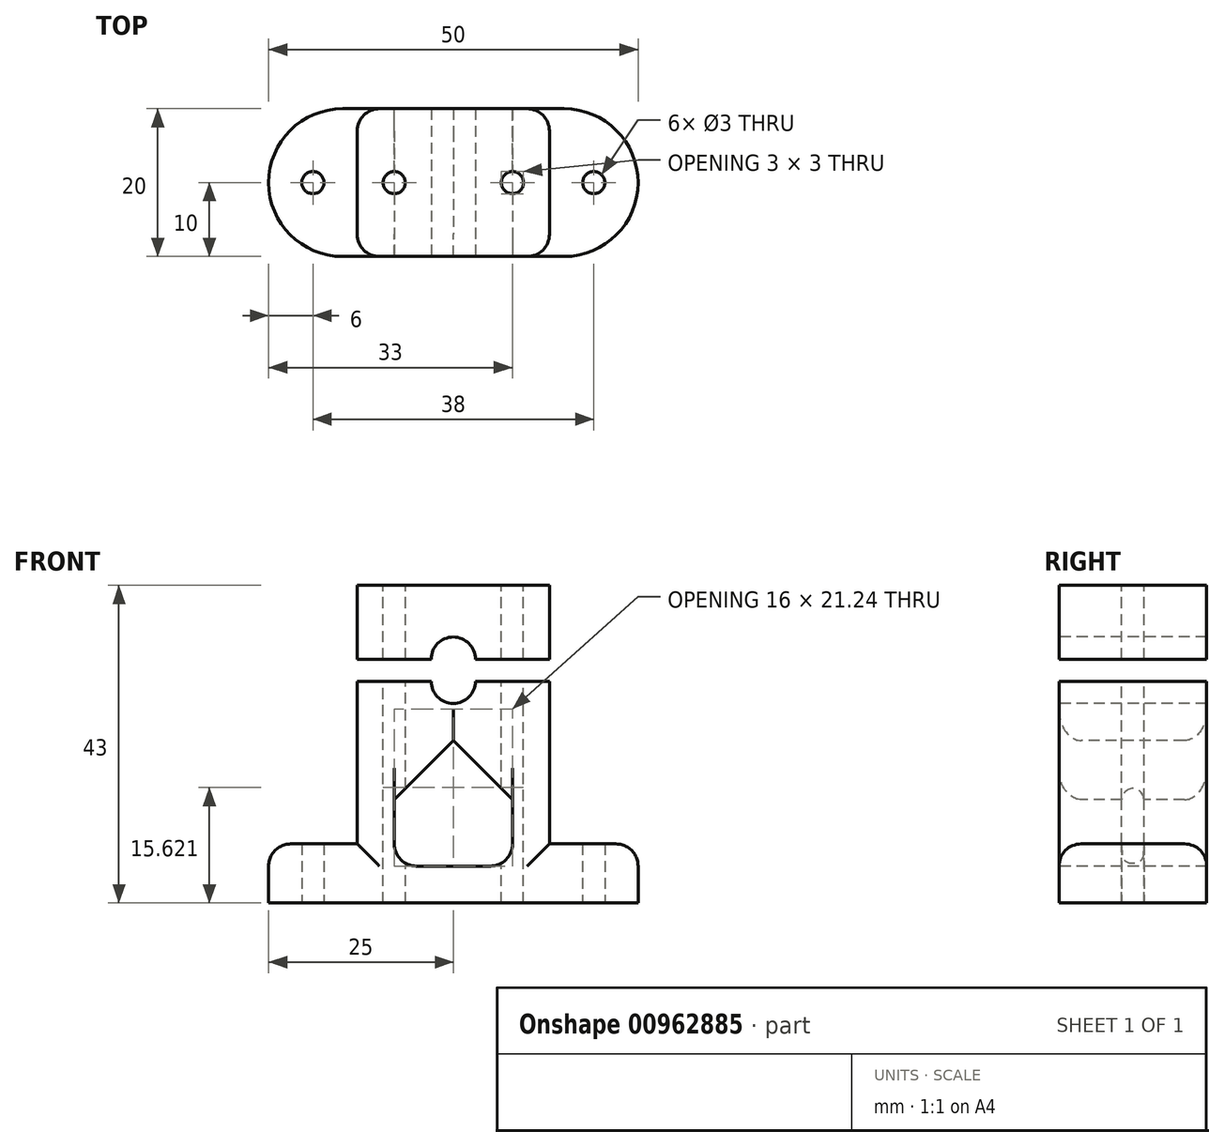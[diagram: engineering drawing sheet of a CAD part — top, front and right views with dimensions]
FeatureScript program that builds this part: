
annotation { "Feature Type Name" : "Feature", "Feature Type Description" : "" }
export const myFeature = defineFeature(function(context is Context, id is Id, definition is map)
    precondition{}
    {
        {
            var Q0;
            Q0=qCreatedBy(makeId("Top.planeOp"),FACE);
            var sketch = newSketch(context, id + "F0", { "sketchPlane" : qUnion([Q0])});
            skLineSegment(sketch, "E0", {"start": v(0, 0) * mm, "end": v(50, 0) * mm});
            skLineSegment(sketch, "E1", {"start": v(50, 0) * mm, "end": v(50, 8) * mm});
            skLineSegment(sketch, "E2", {"start": v(50, 8) * mm, "end": v(38, 8) * mm});
            skLineSegment(sketch, "E3", {"start": v(38, 8) * mm, "end": v(38, 30) * mm});
            skLineSegment(sketch, "E4", {"start": v(38, 30) * mm, "end": v(28, 30) * mm});
            skLineSegment(sketch, "E5", {"start": v(0, 0) * mm, "end": v(0, 8) * mm});
            skLineSegment(sketch, "E6", {"start": v(0, 8) * mm, "end": v(12, 8) * mm});
            skLineSegment(sketch, "E7", {"start": v(12, 8) * mm, "end": v(12, 30) * mm});
            skLineSegment(sketch, "E8", {"start": v(12, 30) * mm, "end": v(22, 30) * mm});
            skArc(sketch, "E9", {"start": v(22, 30) * mm, "mid": v(25, 27) * mm, "end": v(28, 30) * mm});
            skLineSegment(sketch, "E10", {"start": v(25, 30) * mm, "end": v(25, 0) * mm, "construction": true});
            skLineSegment(sketch, "E11", {"start": v(25, 22) * mm, "end": v(33, 14) * mm});
            skLineSegment(sketch, "E12", {"start": v(33, 14) * mm, "end": v(33, 5) * mm});
            skLineSegment(sketch, "E13", {"start": v(33, 5) * mm, "end": v(17, 5) * mm});
            skLineSegment(sketch, "E14", {"start": v(17, 5) * mm, "end": v(17, 14) * mm});
            skLineSegment(sketch, "E15", {"start": v(17, 14) * mm, "end": v(25, 22) * mm});
            skLineSegment(sketch, "E16", {"start": v(12, 33) * mm, "end": v(12, 43) * mm});
            skLineSegment(sketch, "E17", {"start": v(12, 43) * mm, "end": v(38, 43) * mm});
            skLineSegment(sketch, "E18", {"start": v(38, 43) * mm, "end": v(38, 33) * mm});
            skLineSegment(sketch, "E19", {"start": v(38, 33) * mm, "end": v(28, 33) * mm});
            skArc(sketch, "E20", {"start": v(28, 33) * mm, "mid": v(25, 36) * mm, "end": v(22, 33) * mm});
            skLineSegment(sketch, "E21.trimOffspring", {"start": v(22, 33) * mm, "end": v(12, 33) * mm});
            skSolve(sketch);
        }
        {
            var Q0;
            Q0 = qSketchRegion(id + "F0", true);
            extrude(context, id + "F1", {"entities" : qUnion([Q0]), "oppositeDirection" : true, "depth" : 20 * mm, "offsetDistance" : 25 * mm});
        }
        {
            var Q0;
            Q0=makeQuery(id+"F1.opExtrude","SWEPT_FACE",FACE,{"disambiguationData":[OSD([sQuery(id+"F0.wireOp",EDGE,"E0")])]});
            var sketch = newSketch(context, id + "F2", { "sketchPlane" : qUnion([Q0])});
            skCircle(sketch, "E22", {"center": v(6, -10) * mm, "radius": 1.5 * mm});
            skCircle(sketch, "E23", {"center": v(44, -10) * mm, "radius": 1.5 * mm});
            skLineSegment(sketch, "E24", {"start": v(0, -10) * mm, "end": v(50, -10) * mm, "construction": true});
            skSolve(sketch);
        }
        {
            var Q0;
            Q0=makeQuery(id+"F2.imprint","IMPRINT",FACE,{"disambiguationData":[TD([[makeQuery(id+"F2.imprint","IMPRINT",EDGE,{"derivedFrom":sQuery(id+"F2.wireOp",EDGE,"E22")}),1.0]])]});
            var Q1;
            Q1=makeQuery(id+"F2.imprint","IMPRINT",FACE,{"disambiguationData":[TD([[makeQuery(id+"F2.imprint","IMPRINT",EDGE,{"derivedFrom":sQuery(id+"F2.wireOp",EDGE,"E23")}),1.0]])]});
            extrude(context, id + "F3", {"entities" : qUnion([Q0, Q1]), "operationType" : NewBodyOperationType.REMOVE, "endBound" : BoundingType.THROUGH_ALL, "oppositeDirection" : true, "depth" : 25 * mm, "offsetDistance" : 25 * mm});
        }
        {
            var Q0;
            Q0=makeQuery(id+"F1.opExtrude","SWEPT_FACE",FACE,{"disambiguationData":[OSD([sQuery(id+"F0.wireOp",EDGE,"E8")])]});
            var sketch = newSketch(context, id + "F4", { "sketchPlane" : qUnion([Q0])});
            skCircle(sketch, "E25", {"center": v(-17, -10) * mm, "radius": 1.5 * mm});
            skCircle(sketch, "E26", {"center": v(-33, -10) * mm, "radius": 1.5 * mm});
            skLineSegment(sketch, "E27", {"start": v(-12, -10) * mm, "end": v(-38, -10) * mm, "construction": true});
            skSolve(sketch);
        }
        {
            var Q0;
            Q0=makeQuery(id+"F4.imprint","IMPRINT",FACE,{"disambiguationData":[TD([[makeQuery(id+"F4.imprint","IMPRINT",EDGE,{"derivedFrom":sQuery(id+"F4.wireOp",EDGE,"E25")}),1.0]])]});
            var Q1;
            Q1=makeQuery(id+"F4.imprint","IMPRINT",FACE,{"disambiguationData":[TD([[makeQuery(id+"F4.imprint","IMPRINT",EDGE,{"derivedFrom":sQuery(id+"F4.wireOp",EDGE,"E26")}),1.0]])]});
            extrude(context, id + "F5", {"entities" : qUnion([Q0, Q1]), "operationType" : NewBodyOperationType.REMOVE, "endBound" : BoundingType.THROUGH_ALL, "oppositeDirection" : true, "depth" : 25 * mm, "offsetDistance" : 25 * mm, "hasSecondDirection" : true, "secondDirectionBound" : SecondDirectionBoundingType.THROUGH_ALL, "secondDirectionOppositeDirection" : false, "secondDirectionDepth" : 25 * mm});
        }
        {
            var Q0;
            Q0=makeQuery(id+"F1.opExtrude","CAP_EDGE",EDGE,{"disambiguationData":[OSD([sQuery(id+"F0.wireOp",EDGE,"E1")])],"isStart":true});
            var Q1;
            Q1=makeQuery(id+"F1.opExtrude","CAP_EDGE",EDGE,{"disambiguationData":[OSD([sQuery(id+"F0.wireOp",EDGE,"E1")])],"isStart":false});
            var Q2;
            Q2=makeQuery(id+"F1.opExtrude","CAP_EDGE",EDGE,{"disambiguationData":[OSD([sQuery(id+"F0.wireOp",EDGE,"E5")])],"isStart":false});
            var Q3;
            Q3=makeQuery(id+"F1.opExtrude","CAP_EDGE",EDGE,{"disambiguationData":[OSD([sQuery(id+"F0.wireOp",EDGE,"E5")])],"isStart":true});
            fillet(context, id + "F6", {"entities" : qUnion([Q0, Q1, Q2, Q3]), "radius" : 10 * mm, "tangentPropagation" : true, "allowEdgeOverflow" : false});
        }
        {
            var Q0;
            Q0=makeQuery(id+"F6.opFillet","BLEND_EDGE",EDGE,{"blendedFrom":[makeQuery(id+"F1.opExtrude","CAP_EDGE",EDGE,{"disambiguationData":[OSD([sQuery(id+"F0.wireOp",EDGE,"E1")])],"isStart":true}),makeQuery(id+"F1.opExtrude","SWEPT_FACE",FACE,{"disambiguationData":[OSD([sQuery(id+"F0.wireOp",EDGE,"E2")])]})],"blendedInto":[makeQuery(id+"F1.opExtrude","SWEPT_FACE",FACE,{"disambiguationData":[OSD([sQuery(id+"F0.wireOp",EDGE,"E2")])]})]});
            var Q1;
            Q1=makeQuery(id+"F1.opExtrude","CAP_EDGE",EDGE,{"disambiguationData":[OSD([sQuery(id+"F0.wireOp",EDGE,"E3")])],"isStart":false});
            var Q2;
            Q2=makeQuery(id+"F1.opExtrude","CAP_EDGE",EDGE,{"disambiguationData":[OSD([sQuery(id+"F0.wireOp",EDGE,"E3")])],"isStart":true});
            var Q3;
            Q3=makeQuery(id+"F1.opExtrude","CAP_EDGE",EDGE,{"disambiguationData":[OSD([sQuery(id+"F0.wireOp",EDGE,"E7")])],"isStart":false});
            var Q4;
            Q4=makeQuery(id+"F6.opFillet","BLEND_EDGE",EDGE,{"blendedFrom":[makeQuery(id+"F1.opExtrude","CAP_EDGE",EDGE,{"disambiguationData":[OSD([sQuery(id+"F0.wireOp",EDGE,"E5")])],"isStart":true}),makeQuery(id+"F1.opExtrude","SWEPT_FACE",FACE,{"disambiguationData":[OSD([sQuery(id+"F0.wireOp",EDGE,"E6")])]})],"blendedInto":[makeQuery(id+"F1.opExtrude","SWEPT_FACE",FACE,{"disambiguationData":[OSD([sQuery(id+"F0.wireOp",EDGE,"E6")])]})]});
            var Q5;
            Q5=makeQuery(id+"F1.opExtrude","CAP_EDGE",EDGE,{"disambiguationData":[OSD([sQuery(id+"F0.wireOp",EDGE,"E7")])],"isStart":true});
            var Q6;
            {var subQ0=sQuery(id+"F0.wireOp",EDGE,"E14");var subQ1=sQuery(id+"F0.wireOp",EDGE,"E13");Q6=makeQuery(id+"F5.boolean.opBoolean","SPLIT",EDGE,{"disambiguationData":[TD([makeQuery(id+"F1.opExtrude","CAP_FACE",FACE,{"disambiguationData":[OSD([sQuery(id+"F0.wireOp",EDGE,"E0"),sQuery(id+"F0.wireOp",EDGE,"E1"),sQuery(id+"F0.wireOp",EDGE,"E2"),sQuery(id+"F0.wireOp",EDGE,"E3"),sQuery(id+"F0.wireOp",EDGE,"E4"),sQuery(id+"F0.wireOp",EDGE,"E5"),sQuery(id+"F0.wireOp",EDGE,"E6"),sQuery(id+"F0.wireOp",EDGE,"E7"),sQuery(id+"F0.wireOp",EDGE,"E8"),sQuery(id+"F0.wireOp",EDGE,"E9"),sQuery(id+"F0.wireOp",EDGE,"E11"),sQuery(id+"F0.wireOp",EDGE,"E12"),subQ1,subQ0,sQuery(id+"F0.wireOp",EDGE,"E15")])],"isStart":true})])],"derivedFrom":makeQuery(id+"F1.opExtrude","SWEPT_EDGE",EDGE,{"disambiguationData":[OSD([subQ1,subQ0])]})});}
            var Q7;
            {var subQ0=sQuery(id+"F0.wireOp",EDGE,"E13");var subQ1=sQuery(id+"F0.wireOp",EDGE,"E12");Q7=makeQuery(id+"F5.boolean.opBoolean","SPLIT",EDGE,{"disambiguationData":[TD([makeQuery(id+"F1.opExtrude","CAP_FACE",FACE,{"disambiguationData":[OSD([sQuery(id+"F0.wireOp",EDGE,"E0"),sQuery(id+"F0.wireOp",EDGE,"E1"),sQuery(id+"F0.wireOp",EDGE,"E2"),sQuery(id+"F0.wireOp",EDGE,"E3"),sQuery(id+"F0.wireOp",EDGE,"E4"),sQuery(id+"F0.wireOp",EDGE,"E5"),sQuery(id+"F0.wireOp",EDGE,"E6"),sQuery(id+"F0.wireOp",EDGE,"E7"),sQuery(id+"F0.wireOp",EDGE,"E8"),sQuery(id+"F0.wireOp",EDGE,"E9"),sQuery(id+"F0.wireOp",EDGE,"E11"),subQ1,subQ0,sQuery(id+"F0.wireOp",EDGE,"E14"),sQuery(id+"F0.wireOp",EDGE,"E15")])],"isStart":true})])],"derivedFrom":makeQuery(id+"F1.opExtrude","SWEPT_EDGE",EDGE,{"disambiguationData":[OSD([subQ1,subQ0])]})});}
            var Q8;
            Q8=makeQuery(id+"F1.opExtrude","CAP_EDGE",EDGE,{"disambiguationData":[OSD([sQuery(id+"F0.wireOp",EDGE,"E11")])],"isStart":true});
            var Q9;
            Q9=makeQuery(id+"F1.opExtrude","CAP_EDGE",EDGE,{"disambiguationData":[OSD([sQuery(id+"F0.wireOp",EDGE,"E15")])],"isStart":true});
            var Q10;
            Q10=makeQuery(id+"F1.opExtrude","CAP_EDGE",EDGE,{"disambiguationData":[OSD([sQuery(id+"F0.wireOp",EDGE,"E15")])],"isStart":false});
            var Q11;
            Q11=makeQuery(id+"F1.opExtrude","CAP_EDGE",EDGE,{"disambiguationData":[OSD([sQuery(id+"F0.wireOp",EDGE,"E11")])],"isStart":false});
            fillet(context, id + "F7", {"entities" : qUnion([Q0, Q1, Q2, Q3, Q4, Q5, Q6, Q7, Q8, Q9, Q10, Q11]), "radius" : 3 * mm, "tangentPropagation" : true, "allowEdgeOverflow" : false});
        }
        {
            var Q0;
            Q0=makeQuery(id+"F1.opExtrude","SWEPT_BODY",BODY,{"disambiguationData":[OSD([sQuery(id+"F0.wireOp",EDGE,"E0"),sQuery(id+"F0.wireOp",EDGE,"E1"),sQuery(id+"F0.wireOp",EDGE,"E2"),sQuery(id+"F0.wireOp",EDGE,"E3"),sQuery(id+"F0.wireOp",EDGE,"E4"),sQuery(id+"F0.wireOp",EDGE,"E5"),sQuery(id+"F0.wireOp",EDGE,"E6"),sQuery(id+"F0.wireOp",EDGE,"E7"),sQuery(id+"F0.wireOp",EDGE,"E8"),sQuery(id+"F0.wireOp",EDGE,"E9"),sQuery(id+"F0.wireOp",EDGE,"E11"),sQuery(id+"F0.wireOp",EDGE,"E12"),sQuery(id+"F0.wireOp",EDGE,"E13"),sQuery(id+"F0.wireOp",EDGE,"E14"),sQuery(id+"F0.wireOp",EDGE,"E15")])]});
            var Q1;
            Q1=makeQuery(id+"F1.opExtrude","CAP_EDGE",EDGE,{"disambiguationData":[OSD([sQuery(id+"F0.wireOp",EDGE,"E0")])],"isStart":false});
            var Q2;
            Q2=makeQuery(id+"F1.opExtrude","CAP_EDGE",EDGE,{"disambiguationData":[OSD([sQuery(id+"F0.wireOp",EDGE,"E0")])],"isStart":false});
            transform(context, id + "F8", {"entities" : qUnion([Q0]), "transformType" : TransformType.ROTATION, "transformAxis" : qUnion([Q2]), "angle" : 90 * degree, "makeCopy" : false});
        }
        {
            var Q0;
            Q0=makeQuery(id+"F1.opExtrude","SWEPT_BODY",BODY,{"disambiguationData":[OSD([sQuery(id+"F0.wireOp",EDGE,"E16"),sQuery(id+"F0.wireOp",EDGE,"E17"),sQuery(id+"F0.wireOp",EDGE,"E18"),sQuery(id+"F0.wireOp",EDGE,"E19"),sQuery(id+"F0.wireOp",EDGE,"E20"),sQuery(id+"F0.wireOp",EDGE,"E21.trimOffspring")])]});
            var Q1;
            Q1=makeQuery(id+"F1.opExtrude","CAP_EDGE",EDGE,{"disambiguationData":[OSD([sQuery(id+"F0.wireOp",EDGE,"E0")])],"isStart":false});
            transform(context, id + "F9", {"entities" : qUnion([Q0]), "transformType" : TransformType.ROTATION, "transformAxis" : qUnion([Q1]), "angle" : 90 * degree, "makeCopy" : false});
        }
        {
            var Q0;
            Q0=makeQuery(id+"F1.opExtrude","CAP_EDGE",EDGE,{"disambiguationData":[OSD([sQuery(id+"F0.wireOp",EDGE,"E18")])],"isStart":false});
            var Q1;
            Q1=makeQuery(id+"F1.opExtrude","CAP_EDGE",EDGE,{"disambiguationData":[OSD([sQuery(id+"F0.wireOp",EDGE,"E16")])],"isStart":false});
            var Q2;
            Q2=makeQuery(id+"F1.opExtrude","CAP_EDGE",EDGE,{"disambiguationData":[OSD([sQuery(id+"F0.wireOp",EDGE,"E18")])],"isStart":true});
            var Q3;
            Q3=makeQuery(id+"F1.opExtrude","CAP_EDGE",EDGE,{"disambiguationData":[OSD([sQuery(id+"F0.wireOp",EDGE,"E16")])],"isStart":true});
            fillet(context, id + "F10", {"entities" : qUnion([Q0, Q1, Q2, Q3]), "radius" : 3 * mm, "tangentPropagation" : true, "allowEdgeOverflow" : false});
        }
    });
